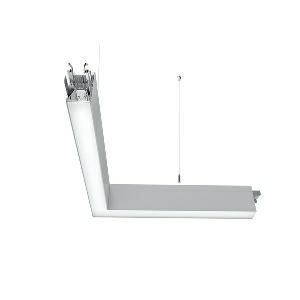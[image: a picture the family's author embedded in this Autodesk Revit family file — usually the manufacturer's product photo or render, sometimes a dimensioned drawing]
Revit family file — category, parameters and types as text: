
# Revit family: idoo_line_-_ilp_3000_vtl_d_lr_mid_00807711_6944
name_source: partatom
category: Lighting Fixtures
units: mm (PartAtom-declared; Revit-internal decimal feet)

## family parameters
Cut with Voids When Loaded = No
Host = Face
Light Source = No
Part Type = Normal
Room Calculation Point = No
Round Connector Dimension = Use Diameter
Shared = No

## types (1)
- IDOO.line - ILP 3000/VTL/D/LR MID (1 x LED, 3150 lm, 2700-6500K)
    Apparent Load = 32 VA
    Approval mark = CE
    CIE Flux Codes = 66 91 98 40 100
    Color Rendering = 90-100
    Color Temperature = 2700-6500K
    Control Gear = Electronic ballast
    Default Elevation = 1800 mm
    Description = ILP 3000/VTL/D|Suspended luminaire|light source: LED|connected load: 220-240 V, 50/60 Hz|Power consumption: approx. 32 W|standby: approx. 0,25|luminous flux: 3150 lm|luminous efficacy: 98 lm/W|light distribution: Direct/indirect|direct ratio: approx. 40 %|colour temperature: Cold white, ca. 2700-6500 K|color rendering index (CRI): >= 90|chromaticity tolerance:  3 SDCM|System of protection: IP 40|technology: Continuously dimmable|luminaire body|material: Sectional aluminium|colour: Silver|lamp cover: Acrylic (PMMA), Clear|Fastening: Steel cable 0.3 - 0.7 m|glare control: Prism aperture|luminance(L65): <= 2700 cd/m|unified glare rating(4H 8H): <=  16|special features: Specified values at approx. 4000 K, DALI Load 1x, Through-wired, up to 18 m on one mains connection, External control required for Dali Device type 8, Flicker-free, Constant luminous flux between 2700 and 6500 K, Constant colour temperature over the whole dimming range, Continous light without dark z, Suitable as emergency lighting, 90░ rerouting on the right sid, Mechanical and electrical connection of the individual modules without tools|
    Frequency = 50 Hz
    Height = 110 mm
    Lamp = 1 x LED
    Lamp Light Flux = 3150 lm
    Lamp count = 1
    Length = 600 mm
    Luminous efficacy = 98 lm/W
    Manufacturer = Waldmann
    ModVariant = No
    Model = 00807711
    Mounting Place = Ceiling
    Mounting Type = Pendant
    Number of Poles = 1
    OnlyDefault = Yes
    Power Factor = 1
    Product Name = IDOO.line - ILP 3000/VTL/D/LR MID
    Product group = Suspended luminaire
    ProductGroupID = 9
    Protection Class = Protection class I
    Protection Degree = IP 40
    RLX_Detail_Level = 1
    RLX_Emergency_Light_Flux = 0 lm
    RLX_Emergency_Type = 0
    RLX_Emergency_Type_DB = No
    RlxData = <blob elided: 22173 chars, md5=0d1803e9>
    Socket = socket
    Standby Power = 0 W
    System Light Flux = 3150 lm
    System Power = 32 W
    Type Comments = Product without accessories
    Type Image = ilp_dlp_lr_si.jpg
    URL = http://relux.com
    VarID = ---
    Voltage = 230 V
    Voltage Range = 220-240 V
    Weight = 0.00 kg
    Width = 600 mm

## geometry (parser evidence)
native form markers: Blend x4, Sweep x14
no freeform markers — native parametric forms only
